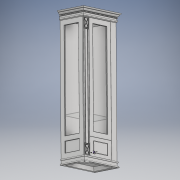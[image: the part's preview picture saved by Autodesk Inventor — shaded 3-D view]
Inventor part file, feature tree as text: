
AUTODESK INVENTOR PART (.ipt)
format: ipt  version: 2019 (Build 230136000, 136)  size: 1,148,928 bytes
history: native  units: mm
features: other x53, projected_geometry x22, sketch x21, extrude x16, fillet x6, pattern_linear x3, shell x2, sweep x2
ambient origin geometry x8: Origin, YZ Plane, XZ Plane, XY Plane, X Axis, Y Axis, Z Axis, Center Point
bodies: Body1 (feature_tree), Body2 (feature_tree), Body3 (feature_tree), Body4 (feature_tree), Body5 (feature_tree), Body6 (feature_tree), Body7 (feature_tree), Body8 (feature_tree), Body9 (feature_tree), Body10 (feature_tree), Body11 (feature_tree), Body12 (feature_tree), Body13 (feature_tree), Body14 (feature_tree), Body15 (feature_tree), Body16 (feature_tree), Body17 (feature_tree), Body18 (feature_tree), Body19 (feature_tree), Body20 (feature_tree), Body21 (feature_tree)
feature tree (125):
  other  "Твердое тело1"
  other  "РабПлоскость3"
  other  "РабПлоскость1"
  other  "РабПлоскость4"
  extrude  "Выдавливание2"  Depth=1996.0mm
  other  "РабПлоскость5"
  other  "Разделение3"
  other  "РабПлоскость6"
  other  "Разделение4"
  other  "РабПлоскость7"
  other  "Разделение5"
  other  "РабПлоскость8"
  other  "Разделение6"
  extrude  "Выдавливание3"  Depth=1996.0mm
  other  "РабПлоскость9"
  other  "РабПлоскость10"
  other  "Разделение7"
  other  "Разделение8"
  other  "Толщина1"
  other  "РабПлоскость11"
  other  "Разделение9"
  other  "Толщина2"
  shell  "Оболочка1"  Thickness=0.0mm
  extrude  "Выдавливание4"  [1 undecoded]
  fillet  "Сопряжение1"  [1 undecoded]
  extrude  "Выдавливание5"  [1 undecoded]
  other  "Толщина3"
  shell  "Оболочка3"  Thickness=-17.4mm
  extrude  "Выдавливание6"  Depth=70.0mm
  fillet  "Сопряжение2"  Radius=150.0mm
  extrude  "Выдавливание7"  Depth=70.0mm
  fillet  "Сопряжение3"  [1 undecoded]
  sketch  "Эскиз8"
  extrude  "Выдавливание8"  [1 undecoded]
  extrude  "Выдавливание9"  [1 undecoded]
  extrude  "Выдавливание10"  Depth=2.0mm
  extrude  "Выдавливание11"  Depth=2.0mm
  extrude  "Выдавливание12"  [1 undecoded]
  extrude  "Выдавливание13"  Depth=2.0mm
  extrude  "Выдавливание14"  Depth=2.0mm
  fillet  "Сопряжение4"  Radius=70.0mm
  sweep  "Сдвиг1"
  extrude  "Выдавливание15"  TaperAngle=0.0deg  [1 undecoded]
  other  "Ball_end_straight:1"
  pattern_linear  "Прямоуг.массив1"  Count1=2  [1 undecoded]
  other  "Ball_end_straight:2"
  pattern_linear  "Прямоуг.массив2"  Count1=4  [1 undecoded]
  other  "Ball_end_straight:3"
  pattern_linear  "Прямоуг.массив3"  Spacing1=32.0mm  [1 undecoded]
  other  "РабПлоскость12"
  extrude  "Выдавливание16"  Depth=32.0mm
  fillet  "Сопряжение5"  Radius=32.0mm
  sketch  "Эскиз20"
  other  "РабПлоскость13"
  sketch  "Эскиз21"
  sweep  "Сдвиг2"
  other  "РабПлоскость14"
  extrude  "Выдавливание17"  Depth=20.0mm TaperAngle=0.0deg
  fillet  "Сопряжение6"  Radius=10.0mm
  sketch  "Эскиз2"
  sketch  "Эскиз3"
  projected_geometry  "Спроецированная петля1"
  sketch  "Эскиз4"
  projected_geometry  "Спроецированная петля2"
  projected_geometry  "Спроецированная петля3"
  other  "Ш1Д Дно"
  sketch  "Эскиз5"
  projected_geometry  "Спроецированная петля4"
  projected_geometry  "Спроецированная петля5"
  other  "Ш1Д Цоколь"
  sketch  "Эскиз6"
  projected_geometry  "Спроецированная петля6"
  other  "Ш1Д Ножка"
  sketch  "Эскиз7"
  projected_geometry  "Спроецированная петля7"
  other  "Ш1Д Планка цоколя"
  projected_geometry  "Спроецированная петля8"
  other  "Ш1Д Филенка бок"
  other  "Ш1Д Стекло бок"
  sketch  "Эскиз9"
  projected_geometry  "Спроецированная петля9"
  other  "Ш1Д Стекло дверцы"
  sketch  "Эскиз10"
  projected_geometry  "Спроецированная петля10"
  projected_geometry  "Спроецированная петля11"
  projected_geometry  "Спроецированная петля12"
  projected_geometry  "Спроецированная петля13"
  other  "Ш1Д Полка"
  sketch  "Эскиз11"
  projected_geometry  "Спроецированная петля14"
  projected_geometry  "Спроецированная петля15"
  other  "Ш1Д Потолок"
  sketch  "Эскиз12"
  projected_geometry  "Спроецированная петля16"
  other  "Ш1Д Цоколь верха"
  sketch  "Эскиз13"
  projected_geometry  "Спроецированная петля17"
  other  "Ш1Д Планка верха"
  sketch  "Эскиз14"
  projected_geometry  "Спроецированная петля18"
  sketch  "3D эскиз1"
  other  "Ш1Д Карниз"
  sketch  "Эскиз15"
  projected_geometry  "Спроецированная петля19"
  other  "Ш1Д Шашечки"
  sketch  "Эскиз19"
  projected_geometry  "Спроецированная петля20"
  other  "Ш1Д Полка стекло"
  projected_geometry  "Спроецированная петля21"
  projected_geometry  "Спроецированная петля22"
  other  "Твердое тело6"
  other  "Твердое тело7"
  other  "Ш1Д Стенка боковая"
  other  "Твердое тело9"
  other  "Твердое тело10"
  other  "Ш1Д Стенка задняя"
  other  "Ш1Д Пилястра"
  other  "Твердое тело13"
  other  "Твердое тело14"
  other  "Твердое тело15"
  other  "Ш1Д Фасад ящика"
  other  "Ш1Д Дверца"
  sketch  "Эскиз16"
  sketch  "Эскиз17"
  sketch  "Эскиз18"
note: 11 required parameter values undecoded (feature->parameter linkage not recoverable at this tier; creation-order binding heuristic only, values carry confidence <= 0.55)
